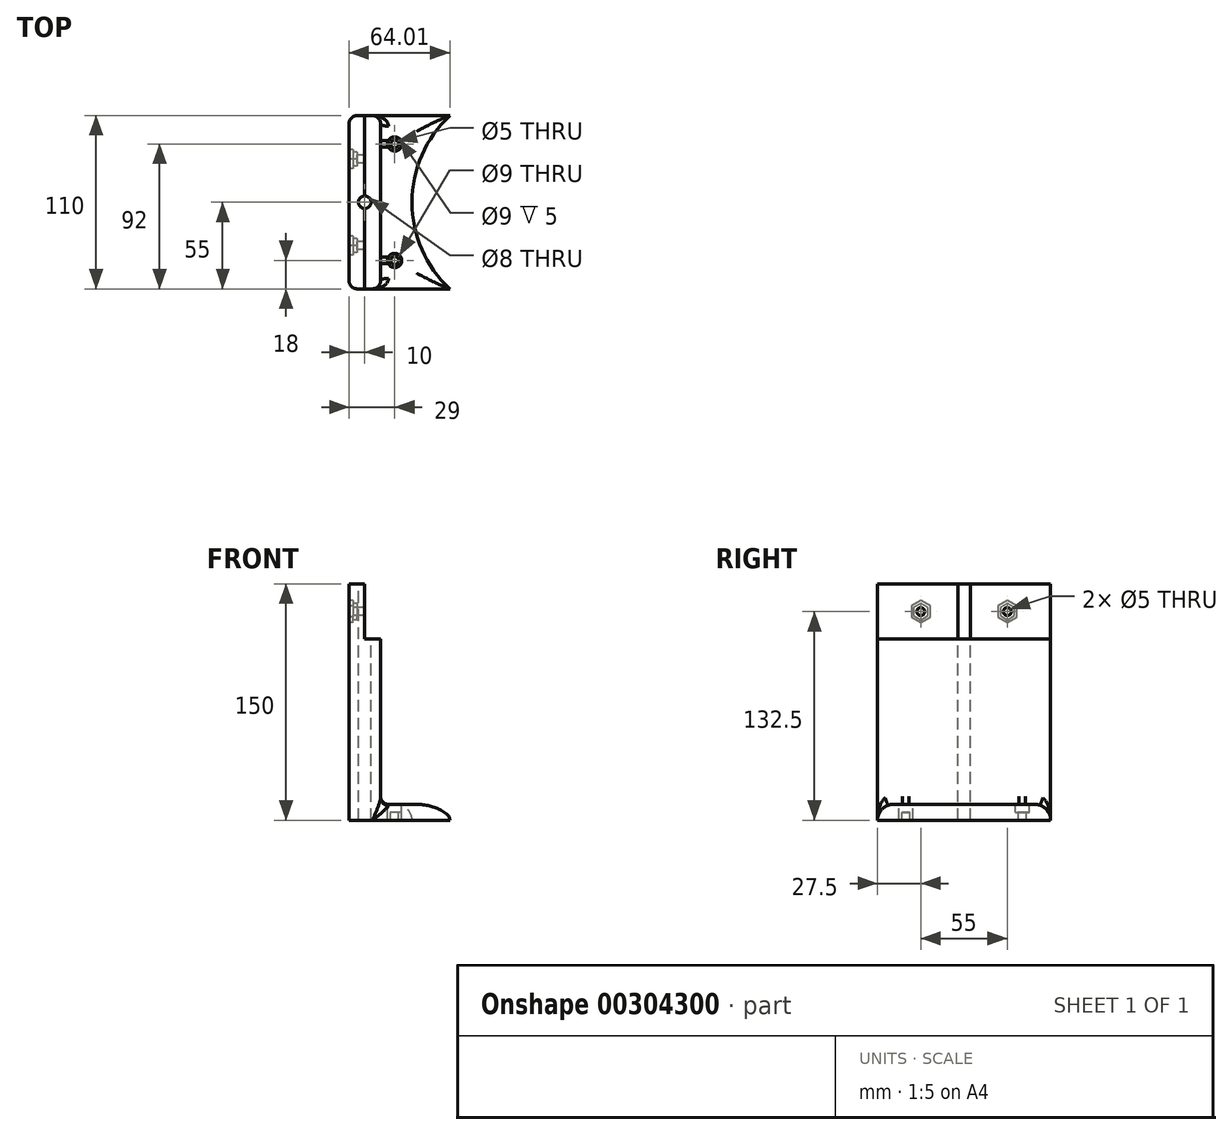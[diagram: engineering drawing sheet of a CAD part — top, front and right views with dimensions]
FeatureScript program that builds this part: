
annotation { "Feature Type Name" : "Feature", "Feature Type Description" : "" }
export const myFeature = defineFeature(function(context is Context, id is Id, definition is map)
    precondition{}
    {
        {
            var Q0;
            Q0=qCreatedBy(makeId("Top.planeOp"),FACE);
            var sketch = newSketch(context, id + "F0", { "sketchPlane" : qUnion([Q0])});
            skCircle(sketch, "E0", {"center": v(0, 0) * mm, "radius": 85 * mm});
            skLineSegment(sketch, "E1", {"start": v(0, 55) * mm, "end": v(-115, 55) * mm});
            skLineSegment(sketch, "E2", {"start": v(-115, 55) * mm, "end": v(-115, -55) * mm});
            skLineSegment(sketch, "E3", {"start": v(-115, -55) * mm, "end": v(0, -55) * mm});
            skLineSegment(sketch, "E4", {"start": v(-95, 55) * mm, "end": v(-95, -55) * mm});
            skCircle(sketch, "E5", {"center": v(0, 0) * mm, "radius": 75 * mm});
            skSolve(sketch);
        }
        {
            var Q0;
            {var subQ0=sQuery(id+"F0.wireOp",EDGE,"E2");Q0=makeQuery(id+"F0.imprint","IMPRINT",FACE,{"disambiguationData":[TD([[makeQuery(id+"F0.imprint","IMPRINT",EDGE,{"derivedFrom":subQ0}),1.0]])]});}
            extrude(context, id + "F1", {"entities" : qUnion([Q0]), "depth" : 150 * mm});
        }
        {
            var Q0;
            {var subQ5=sQuery(id+"F0.wireOp",EDGE,"E4");Q0=makeQuery(id+"F0.imprint","IMPRINT",FACE,{"disambiguationData":[TD([[makeQuery(id+"F0.imprint","IMPRINT",EDGE,{"derivedFrom":subQ5}),1.0]])]});}
            var Q1;
            {var subQ0=sQuery(id+"F0.wireOp",EDGE,"E1");var subQ1=sQuery(id+"F0.wireOp",EDGE,"E0");var subQ2=makeQuery(id+"F0.imprint","INTERSECT",VERTEX,{"derivedFrom":[subQ1,subQ0]});Q1=makeQuery(id+"F0.imprint","IMPRINT",FACE,{"disambiguationData":[TD([[makeQuery(id+"F0.imprint","IMPRINT",EDGE,{"disambiguationData":[TD([[subQ2,-1.0]])],"derivedFrom":subQ1}),1.0]])]});}
            extrude(context, id + "F2", {"entities" : qUnion([Q0, Q1]), "operationType" : NewBodyOperationType.ADD, "depth" : 10 * mm});
        }
        {
            var Q0;
            Q0=makeQuery(id+"F2.opExtrude","CAP_EDGE",EDGE,{"disambiguationData":[OSD([sQuery(id+"F0.wireOp",EDGE,"E3")])],"isStart":false});
            var Q1;
            Q1=makeQuery(id+"F2.opExtrude","CAP_EDGE",EDGE,{"disambiguationData":[OSD([sQuery(id+"F0.wireOp",EDGE,"E5")])],"isStart":false});
            var Q2;
            Q2=makeQuery(id+"F2.opExtrude","CAP_EDGE",EDGE,{"disambiguationData":[OSD([sQuery(id+"F0.wireOp",EDGE,"E1")])],"isStart":false});
            fillet(context, id + "F3", {"entities" : qUnion([Q0, Q1, Q2]), "radius" : 10 * mm, "tangentPropagation" : true, "allowEdgeOverflow" : false});
        }
        {
            var Q0;
            Q0=makeQuery(id+"F2.opExtrude","CAP_FACE",FACE,{"disambiguationData":[OSD([sQuery(id+"F0.wireOp",EDGE,"E1"),sQuery(id+"F0.wireOp",EDGE,"E3"),sQuery(id+"F0.wireOp",EDGE,"E4"),sQuery(id+"F0.wireOp",EDGE,"E5")])],"isStart":false});
            var sketch = newSketch(context, id + "F4", { "sketchPlane" : qUnion([Q0])});
            skCircle(sketch, "E6", {"center": v(-86, 37) * mm, "radius": 4.5 * mm});
            skCircle(sketch, "E7", {"center": v(-86, 37) * mm, "radius": 2.5 * mm});
            skCircle(sketch, "E8.MirrorC", {"center": v(-86, -37) * mm, "radius": 2.5 * mm});
            skCircle(sketch, "E9.MirrorC", {"center": v(-86, -37) * mm, "radius": 4.5 * mm});
            skSolve(sketch);
        }
        {
            var Q0;
            Q0=makeQuery(id+"F4.imprint","IMPRINT",FACE,{"disambiguationData":[TD([[makeQuery(id+"F4.imprint","IMPRINT",EDGE,{"derivedFrom":sQuery(id+"F4.wireOp",EDGE,"E7")}),1.0]])]});
            var Q1;
            Q1=makeQuery(id+"F4.imprint","IMPRINT",FACE,{"disambiguationData":[TD([[makeQuery(id+"F4.imprint","IMPRINT",EDGE,{"derivedFrom":sQuery(id+"F4.wireOp",EDGE,"E8.MirrorC")}),-1.0]])]});
            extrude(context, id + "F5", {"entities" : qUnion([Q0, Q1]), "operationType" : NewBodyOperationType.REMOVE, "oppositeDirection" : true, "depth" : 10 * mm});
        }
        {
            var Q0;
            Q0=makeQuery(id+"F4.imprint","IMPRINT",FACE,{"disambiguationData":[TD([[makeQuery(id+"F4.imprint","IMPRINT",EDGE,{"derivedFrom":sQuery(id+"F4.wireOp",EDGE,"E6")}),1.0]])]});
            var Q1;
            Q1=makeQuery(id+"F4.imprint","IMPRINT",FACE,{"disambiguationData":[TD([[makeQuery(id+"F4.imprint","IMPRINT",EDGE,{"derivedFrom":sQuery(id+"F4.wireOp",EDGE,"E8.MirrorC")}),1.0]])]});
            extrude(context, id + "F6", {"entities" : qUnion([Q0, Q1]), "operationType" : NewBodyOperationType.REMOVE, "oppositeDirection" : true, "depth" : 5 * mm});
        }
        {
            var Q0;
            Q0=makeQuery(id+"F1.opExtrude","CAP_FACE",FACE,{"disambiguationData":[OSD([sQuery(id+"F0.wireOp",EDGE,"E1"),sQuery(id+"F0.wireOp",EDGE,"E2"),sQuery(id+"F0.wireOp",EDGE,"E3"),sQuery(id+"F0.wireOp",EDGE,"E4")])],"isStart":false});
            var sketch = newSketch(context, id + "F7", { "sketchPlane" : qUnion([Q0])});
            skLineSegment(sketch, "E10", {"start": v(-95, -55) * mm, "end": v(-95, 55) * mm});
            skLineSegment(sketch, "E11", {"start": v(-95, 55) * mm, "end": v(-105, 55) * mm});
            skLineSegment(sketch, "E12", {"start": v(-105, 55) * mm, "end": v(-105, -55) * mm});
            skLineSegment(sketch, "E13", {"start": v(-105, -55) * mm, "end": v(-95, -55) * mm});
            skSolve(sketch);
        }
        {
            var Q0;
            Q0=makeQuery(id+"F7.imprint","IMPRINT",FACE,{"disambiguationData":[TD([[makeQuery(id+"F7.imprint","IMPRINT",EDGE,{"derivedFrom":sQuery(id+"F7.wireOp",EDGE,"E10")}),-1.0]])]});
            extrude(context, id + "F8", {"entities" : qUnion([Q0]), "operationType" : NewBodyOperationType.REMOVE, "oppositeDirection" : true, "depth" : 35 * mm});
        }
        {
            var Q0;
            Q0=makeQuery(id+"F1.opExtrude","CAP_FACE",FACE,{"disambiguationData":[OSD([sQuery(id+"F0.wireOp",EDGE,"E1"),sQuery(id+"F0.wireOp",EDGE,"E2"),sQuery(id+"F0.wireOp",EDGE,"E3"),sQuery(id+"F0.wireOp",EDGE,"E4")])],"isStart":false});
            var sketch = newSketch(context, id + "F9", { "sketchPlane" : qUnion([Q0])});
            skCircle(sketch, "E14", {"center": v(-105, 0) * mm, "radius": 4 * mm});
            skSolve(sketch);
        }
        {
            var Q0;
            {var subQ0=sQuery(id+"F9.wireOp",EDGE,"E14");var subQ1=makeQuery(id+"F8.boolean.opBoolean","COPY",EDGE,{"derivedFrom":makeQuery(id+"F8.opExtrude","CAP_EDGE",EDGE,{"disambiguationData":[OSD([sQuery(id+"F7.wireOp",EDGE,"E12")])],"isStart":true})});var subQ2=makeQuery(id+"F9.imprint","INTERSECT",VERTEX,{"disambiguationData":[OD(0.0)],"derivedFrom":[subQ1,subQ0]});Q0=makeQuery(id+"F9.imprint","IMPRINT",FACE,{"disambiguationData":[TD([[makeQuery(id+"F9.imprint","IMPRINT",EDGE,{"disambiguationData":[TD([[subQ2,-1.0]])],"derivedFrom":subQ0}),1.0]])]});}
            var Q1;
            {var subQ0=sQuery(id+"F9.wireOp",EDGE,"E14");var subQ1=makeQuery(id+"F8.boolean.opBoolean","COPY",EDGE,{"derivedFrom":makeQuery(id+"F8.opExtrude","CAP_EDGE",EDGE,{"disambiguationData":[OSD([sQuery(id+"F7.wireOp",EDGE,"E12")])],"isStart":true})});var subQ2=makeQuery(id+"F9.imprint","INTERSECT",VERTEX,{"disambiguationData":[OD(0.0)],"derivedFrom":[subQ1,subQ0]});Q1=makeQuery(id+"F9.imprint","IMPRINT",FACE,{"disambiguationData":[TD([[makeQuery(id+"F9.imprint","IMPRINT",EDGE,{"disambiguationData":[TD([[subQ2,1.0]])],"derivedFrom":subQ0}),1.0]])]});}
            extrude(context, id + "F10", {"entities" : qUnion([Q0, Q1]), "operationType" : NewBodyOperationType.REMOVE, "oppositeDirection" : true, "depth" : 150 * mm});
        }
        {
            var Q0;
            Q0=makeQuery(id+"F1.opExtrude","SWEPT_FACE",FACE,{"disambiguationData":[OSD([sQuery(id+"F0.wireOp",EDGE,"E2")])]});
            var sketch = newSketch(context, id + "F11", { "sketchPlane" : qUnion([Q0])});
            skCircle(sketch, "E15.cCircle", {"center": v(-27.5, 132.5) * mm, "radius": 4.5 * mm, "construction": true});
            skLineSegment(sketch, "E15.0", {"start": v(-23, 135.1) * mm, "end": v(-23, 129.9) * mm});
            skLineSegment(sketch, "E15.1", {"start": v(-23, 129.9) * mm, "end": v(-27.5, 127.3) * mm});
            skLineSegment(sketch, "E15.2", {"start": v(-27.5, 127.3) * mm, "end": v(-32, 129.9) * mm});
            skLineSegment(sketch, "E15.3", {"start": v(-32, 129.9) * mm, "end": v(-32, 135.1) * mm});
            skLineSegment(sketch, "E15.4", {"start": v(-32, 135.1) * mm, "end": v(-27.5, 137.7) * mm});
            skLineSegment(sketch, "E15.5", {"start": v(-27.5, 137.7) * mm, "end": v(-23, 135.1) * mm});
            skPoint(sketch, "E15.0.midPoint", {"position": v(-23, 132.5) * mm});
            skLineSegment(sketch, "E16", {"start": v(0, 150) * mm, "end": v(0, 114.74) * mm});
            skCircle(sketch, "E17.cCircle", {"center": v(27.5, 132.5) * mm, "radius": 4.5 * mm, "construction": true});
            skLineSegment(sketch, "E17.0", {"start": v(32, 135.1) * mm, "end": v(32, 129.9) * mm});
            skLineSegment(sketch, "E17.1", {"start": v(32, 129.9) * mm, "end": v(27.5, 127.3) * mm});
            skLineSegment(sketch, "E17.2", {"start": v(27.5, 127.3) * mm, "end": v(23, 129.9) * mm});
            skLineSegment(sketch, "E17.3", {"start": v(23, 129.9) * mm, "end": v(23, 135.1) * mm});
            skLineSegment(sketch, "E17.4", {"start": v(23, 135.1) * mm, "end": v(27.5, 137.7) * mm});
            skLineSegment(sketch, "E17.5", {"start": v(27.5, 137.7) * mm, "end": v(32, 135.1) * mm});
            skPoint(sketch, "E17.0.midPoint", {"position": v(32, 132.5) * mm});
            skCircle(sketch, "E18", {"center": v(-27.5, 132.5) * mm, "radius": 2.5 * mm});
            skCircle(sketch, "E19", {"center": v(27.5, 132.5) * mm, "radius": 2.5 * mm});
            skCircle(sketch, "E20.cCircle", {"center": v(-27.5, 132.5) * mm, "radius": 6 * mm, "construction": true});
            skLineSegment(sketch, "E20.0", {"start": v(-21.5, 135.96) * mm, "end": v(-21.5, 129.04) * mm});
            skLineSegment(sketch, "E20.1", {"start": v(-21.5, 129.04) * mm, "end": v(-27.5, 125.57) * mm});
            skLineSegment(sketch, "E20.2", {"start": v(-27.5, 125.57) * mm, "end": v(-33.5, 129.04) * mm});
            skLineSegment(sketch, "E20.3", {"start": v(-33.5, 129.04) * mm, "end": v(-33.5, 135.96) * mm});
            skLineSegment(sketch, "E20.4", {"start": v(-33.5, 135.96) * mm, "end": v(-27.5, 139.43) * mm});
            skLineSegment(sketch, "E20.5", {"start": v(-27.5, 139.43) * mm, "end": v(-21.5, 135.96) * mm});
            skPoint(sketch, "E20.0.midPoint", {"position": v(-21.5, 132.5) * mm});
            skCircle(sketch, "E21.cCircle", {"center": v(27.5, 132.5) * mm, "radius": 6 * mm, "construction": true});
            skLineSegment(sketch, "E21.0", {"start": v(33.5, 135.96) * mm, "end": v(33.5, 129.04) * mm});
            skLineSegment(sketch, "E21.1", {"start": v(33.5, 129.04) * mm, "end": v(27.5, 125.57) * mm});
            skLineSegment(sketch, "E21.2", {"start": v(27.5, 125.57) * mm, "end": v(21.5, 129.04) * mm});
            skLineSegment(sketch, "E21.3", {"start": v(21.5, 129.04) * mm, "end": v(21.5, 135.96) * mm});
            skLineSegment(sketch, "E21.4", {"start": v(21.5, 135.96) * mm, "end": v(27.5, 139.43) * mm});
            skLineSegment(sketch, "E21.5", {"start": v(27.5, 139.43) * mm, "end": v(33.5, 135.96) * mm});
            skPoint(sketch, "E21.0.midPoint", {"position": v(33.5, 132.5) * mm});
            skSolve(sketch);
        }
        {
            var Q0;
            Q0=makeQuery(id+"F11.imprint","IMPRINT",FACE,{"disambiguationData":[TD([[makeQuery(id+"F11.imprint","IMPRINT",EDGE,{"derivedFrom":sQuery(id+"F11.wireOp",EDGE,"E18")}),1.0]])]});
            var Q1;
            Q1=makeQuery(id+"F11.imprint","IMPRINT",FACE,{"disambiguationData":[TD([[makeQuery(id+"F11.imprint","IMPRINT",EDGE,{"derivedFrom":sQuery(id+"F11.wireOp",EDGE,"E19")}),1.0]])]});
            extrude(context, id + "F12", {"entities" : qUnion([Q0, Q1]), "operationType" : NewBodyOperationType.REMOVE, "oppositeDirection" : true, "depth" : 10 * mm});
        }
        {
            var Q0;
            Q0=makeQuery(id+"F11.imprint","IMPRINT",FACE,{"disambiguationData":[TD([[makeQuery(id+"F11.imprint","IMPRINT",EDGE,{"derivedFrom":sQuery(id+"F11.wireOp",EDGE,"E15.0")}),-1.0]])]});
            var Q1;
            Q1=makeQuery(id+"F11.imprint","IMPRINT",FACE,{"disambiguationData":[TD([[makeQuery(id+"F11.imprint","IMPRINT",EDGE,{"derivedFrom":sQuery(id+"F11.wireOp",EDGE,"E17.0")}),-1.0]])]});
            extrude(context, id + "F13", {"entities" : qUnion([Q0, Q1]), "operationType" : NewBodyOperationType.REMOVE, "oppositeDirection" : true, "depth" : 5.2 * mm});
        }
        {
            var Q0;
            Q0=makeQuery(id+"F11.imprint","IMPRINT",FACE,{"disambiguationData":[TD([[makeQuery(id+"F11.imprint","IMPRINT",EDGE,{"derivedFrom":sQuery(id+"F11.wireOp",EDGE,"E15.0")}),1.0]])]});
            var Q1;
            Q1=makeQuery(id+"F11.imprint","IMPRINT",FACE,{"disambiguationData":[TD([[makeQuery(id+"F11.imprint","IMPRINT",EDGE,{"derivedFrom":sQuery(id+"F11.wireOp",EDGE,"E17.0")}),1.0]])]});
            extrude(context, id + "F14", {"entities" : qUnion([Q0, Q1]), "operationType" : NewBodyOperationType.REMOVE, "oppositeDirection" : true, "depth" : 2.5 * mm});
        }
        {
            var Q0;
            Q0=makeQuery(id+"F1.opExtrude","SWEPT_EDGE",EDGE,{"disambiguationData":[OSD([sQuery(id+"F0.wireOp",EDGE,"E2"),sQuery(id+"F0.wireOp",EDGE,"E3")])]});
            var Q1;
            Q1=makeQuery(id+"F1.opExtrude","SWEPT_EDGE",EDGE,{"disambiguationData":[OSD([sQuery(id+"F0.wireOp",EDGE,"E1"),sQuery(id+"F0.wireOp",EDGE,"E2")])]});
            var Q2;
            Q2=makeQuery(id+"F1.opExtrude","SWEPT_EDGE",EDGE,{"disambiguationData":[OSD([sQuery(id+"F0.wireOp",EDGE,"E3"),sQuery(id+"F0.wireOp",EDGE,"E4")])]});
            var Q3;
            Q3=makeQuery(id+"F1.opExtrude","SWEPT_EDGE",EDGE,{"disambiguationData":[OSD([sQuery(id+"F0.wireOp",EDGE,"E1"),sQuery(id+"F0.wireOp",EDGE,"E4")])]});
            fillet(context, id + "F15", {"entities" : qUnion([Q0, Q1, Q2, Q3]), "radius" : 5 * mm, "tangentPropagation" : true, "allowEdgeOverflow" : false});
        }
        {
            var Q0;
            Q0=makeQuery(id+"F2.opExtrude","CAP_EDGE",EDGE,{"disambiguationData":[OSD([sQuery(id+"F0.wireOp",EDGE,"E4")])],"isStart":false});
            var Q1;
            Q1=makeQuery(id+"F3.opFillet","BLEND_EDGE",EDGE,{"blendedFrom":[makeQuery(id+"F2.opExtrude","CAP_EDGE",EDGE,{"disambiguationData":[OSD([sQuery(id+"F0.wireOp",EDGE,"E1")])],"isStart":false}),makeQuery(id+"F1.opExtrude","SWEPT_FACE",FACE,{"disambiguationData":[OSD([sQuery(id+"F0.wireOp",EDGE,"E4")])]})],"blendedInto":[makeQuery(id+"F1.opExtrude","SWEPT_FACE",FACE,{"disambiguationData":[OSD([sQuery(id+"F0.wireOp",EDGE,"E4")])]})]});
            var Q2;
            Q2=makeQuery(id+"F3.opFillet","BLEND_EDGE",EDGE,{"blendedFrom":[makeQuery(id+"F2.opExtrude","CAP_EDGE",EDGE,{"disambiguationData":[OSD([sQuery(id+"F0.wireOp",EDGE,"E3")])],"isStart":false}),makeQuery(id+"F1.opExtrude","SWEPT_FACE",FACE,{"disambiguationData":[OSD([sQuery(id+"F0.wireOp",EDGE,"E4")])]})],"blendedInto":[makeQuery(id+"F1.opExtrude","SWEPT_FACE",FACE,{"disambiguationData":[OSD([sQuery(id+"F0.wireOp",EDGE,"E4")])]})]});
            fillet(context, id + "F16", {"entities" : qUnion([Q0, Q1, Q2]), "radius" : 5 * mm, "tangentPropagation" : true, "allowEdgeOverflow" : false});
        }
    });
